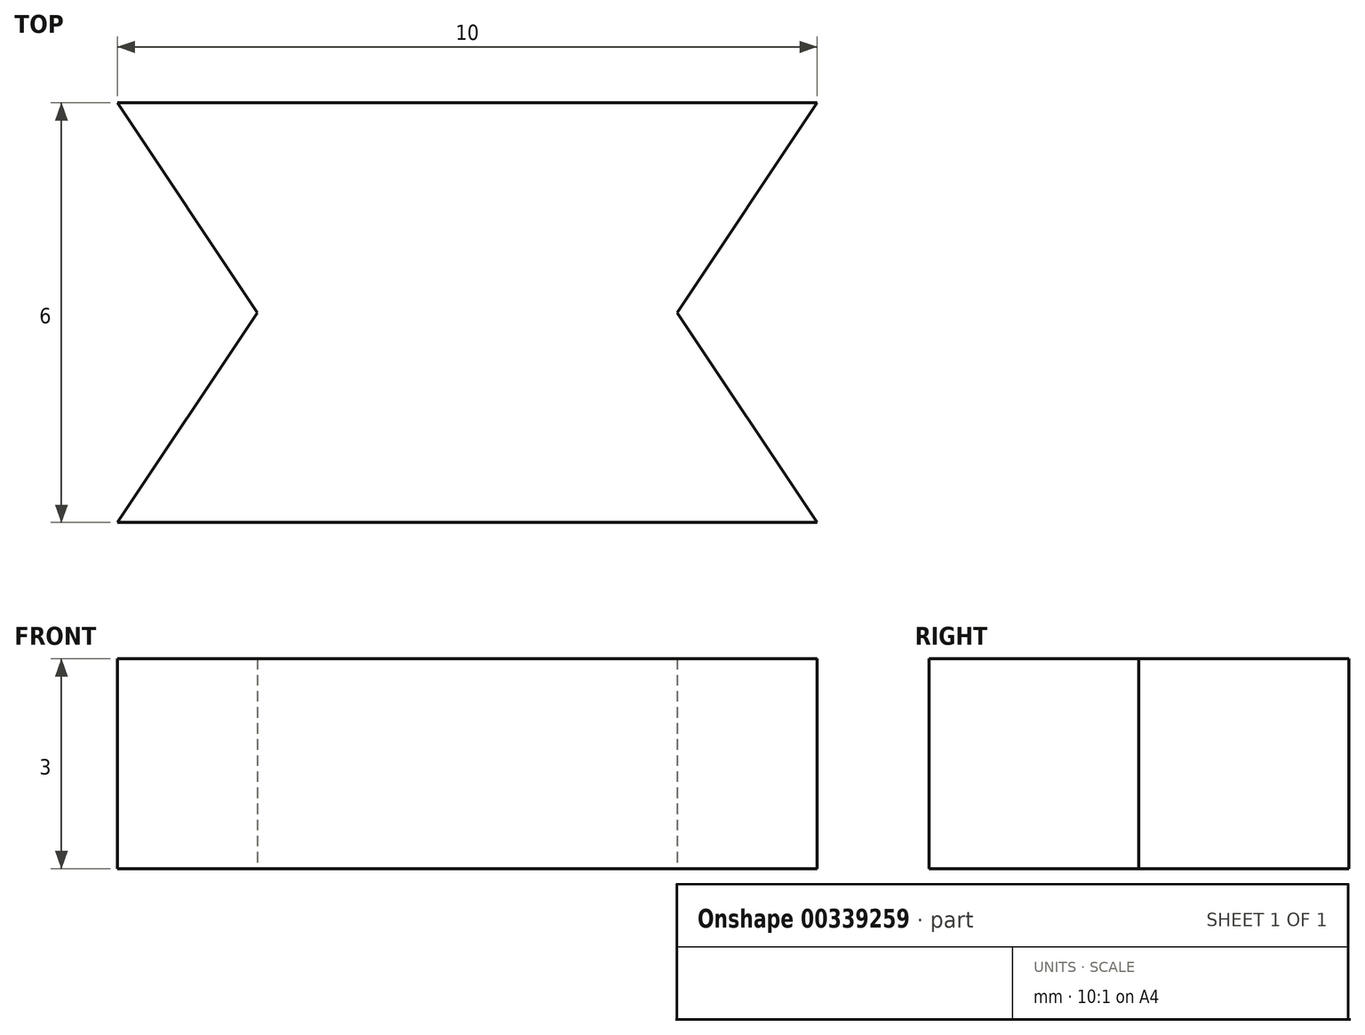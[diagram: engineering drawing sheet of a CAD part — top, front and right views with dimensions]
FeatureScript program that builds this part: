
annotation { "Feature Type Name" : "Feature", "Feature Type Description" : "" }
export const myFeature = defineFeature(function(context is Context, id is Id, definition is map)
    precondition{}
    {
        {
            var Q0;
            Q0=qCreatedBy(makeId("Top.planeOp"),FACE);
            var sketch = newSketch(context, id + "F0", { "sketchPlane" : qUnion([Q0])});
            skLineSegment(sketch, "E0", {"start": v(0, 0) * mm, "end": v(3, 0) * mm});
            skLineSegment(sketch, "E1", {"start": v(3, 0) * mm, "end": v(5, -3) * mm});
            skLineSegment(sketch, "E2", {"start": v(5, -3) * mm, "end": v(-5, -3) * mm});
            skLineSegment(sketch, "E3", {"start": v(-5, -3) * mm, "end": v(-3, 0) * mm});
            skLineSegment(sketch, "E4", {"start": v(-3, 0) * mm, "end": v(0, 0) * mm});
            skLineSegment(sketch, "E5", {"start": v(3, 0) * mm, "end": v(5, 3) * mm});
            skLineSegment(sketch, "E6", {"start": v(5, 3) * mm, "end": v(-5, 3) * mm});
            skLineSegment(sketch, "E7", {"start": v(-5, 3) * mm, "end": v(-3, 0) * mm});
            skSolve(sketch);
        }
        {
            var Q0;
            Q0 = qSketchRegion(id + "F0", true);
            extrude(context, id + "F1", {"entities" : qUnion([Q0]), "depth" : 3 * mm});
        }
    });
